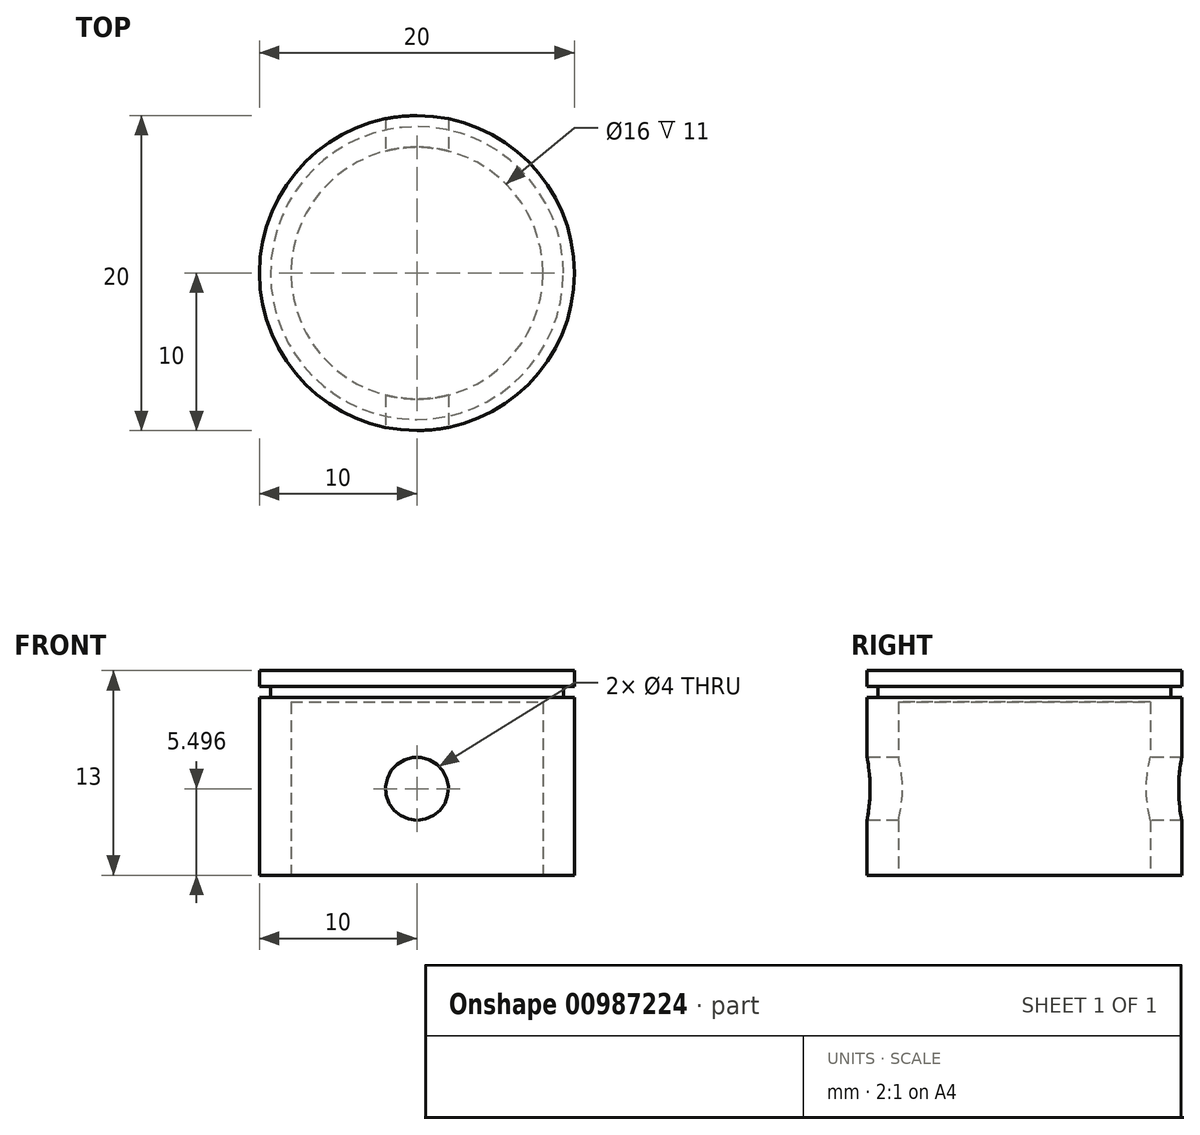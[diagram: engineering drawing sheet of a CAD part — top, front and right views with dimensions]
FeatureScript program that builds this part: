
annotation { "Feature Type Name" : "Feature", "Feature Type Description" : "" }
export const myFeature = defineFeature(function(context is Context, id is Id, definition is map)
    precondition{}
    {
        {
            var Q0;
            Q0=qCreatedBy(makeId("Front.planeOp"),FACE);
            var sketch = newSketch(context, id + "F0", { "sketchPlane" : qUnion([Q0])});
            skLineSegment(sketch, "E0", {"start": v(0, 0) * mm, "end": v(0, 18.65) * mm, "construction": true});
            skLineSegment(sketch, "E1", {"start": v(0, 14.75) * mm, "end": v(10, 14.75) * mm});
            skLineSegment(sketch, "E2", {"start": v(10, 14.75) * mm, "end": v(10, 1.75) * mm});
            skLineSegment(sketch, "E3", {"start": v(10, 1.75) * mm, "end": v(8, 1.75) * mm});
            skLineSegment(sketch, "E4", {"start": v(8, 1.75) * mm, "end": v(8, 12.75) * mm});
            skLineSegment(sketch, "E5", {"start": v(8, 12.75) * mm, "end": v(0, 12.75) * mm});
            skLineSegment(sketch, "E6", {"start": v(0, 12.75) * mm, "end": v(0, 14.75) * mm});
            skCircle(sketch, "E7", {"center": v(0, 7.25) * mm, "radius": 2 * mm});
            skLineSegment(sketch, "E8.bottom", {"start": v(10, 13.75) * mm, "end": v(9.3, 13.75) * mm});
            skLineSegment(sketch, "E8.top", {"start": v(10, 13.05) * mm, "end": v(9.3, 13.05) * mm});
            skLineSegment(sketch, "E8.left", {"start": v(10, 13.75) * mm, "end": v(10, 13.05) * mm});
            skLineSegment(sketch, "E8.right", {"start": v(9.3, 13.75) * mm, "end": v(9.3, 13.05) * mm});
            skLineSegment(sketch, "E9", {"start": v(0, 7.25) * mm, "end": v(8, 7.25) * mm, "construction": true});
            skSolve(sketch);
        }
        {
            var Q0;
            Q0=makeQuery(id+"F0.imprint","IMPRINT",FACE,{"disambiguationData":[TD([[makeQuery(id+"F0.imprint","IMPRINT",EDGE,{"derivedFrom":sQuery(id+"F0.wireOp",EDGE,"E1")}),-1.0]])]});
            var Q1;
            Q1=sQuery(id+"F0.wireOp",EDGE,"E0");
            revolve(context, id + "F1", {"surfaceOperationType" : NewSurfaceOperationType.NEW, "entities" : qUnion([Q0]), "axis" : qUnion([Q1]), "revolveType" : RevolveType.FULL});
        }
        {
            var Q0;
            Q0=makeQuery(id+"F0.imprint","IMPRINT",FACE,{"disambiguationData":[TD([[makeQuery(id+"F0.imprint","IMPRINT",EDGE,{"derivedFrom":sQuery(id+"F0.wireOp",EDGE,"E7")}),1.0]])]});
            extrude(context, id + "F2", {"entities" : qUnion([Q0]), "operationType" : NewBodyOperationType.REMOVE, "endBound" : BoundingType.THROUGH_ALL, "oppositeDirection" : true, "depth" : 25 * mm, "offsetDistance" : 25 * mm, "hasSecondDirection" : true, "secondDirectionBound" : SecondDirectionBoundingType.THROUGH_ALL, "secondDirectionOppositeDirection" : false, "secondDirectionDepth" : 25 * mm});
        }
    });
